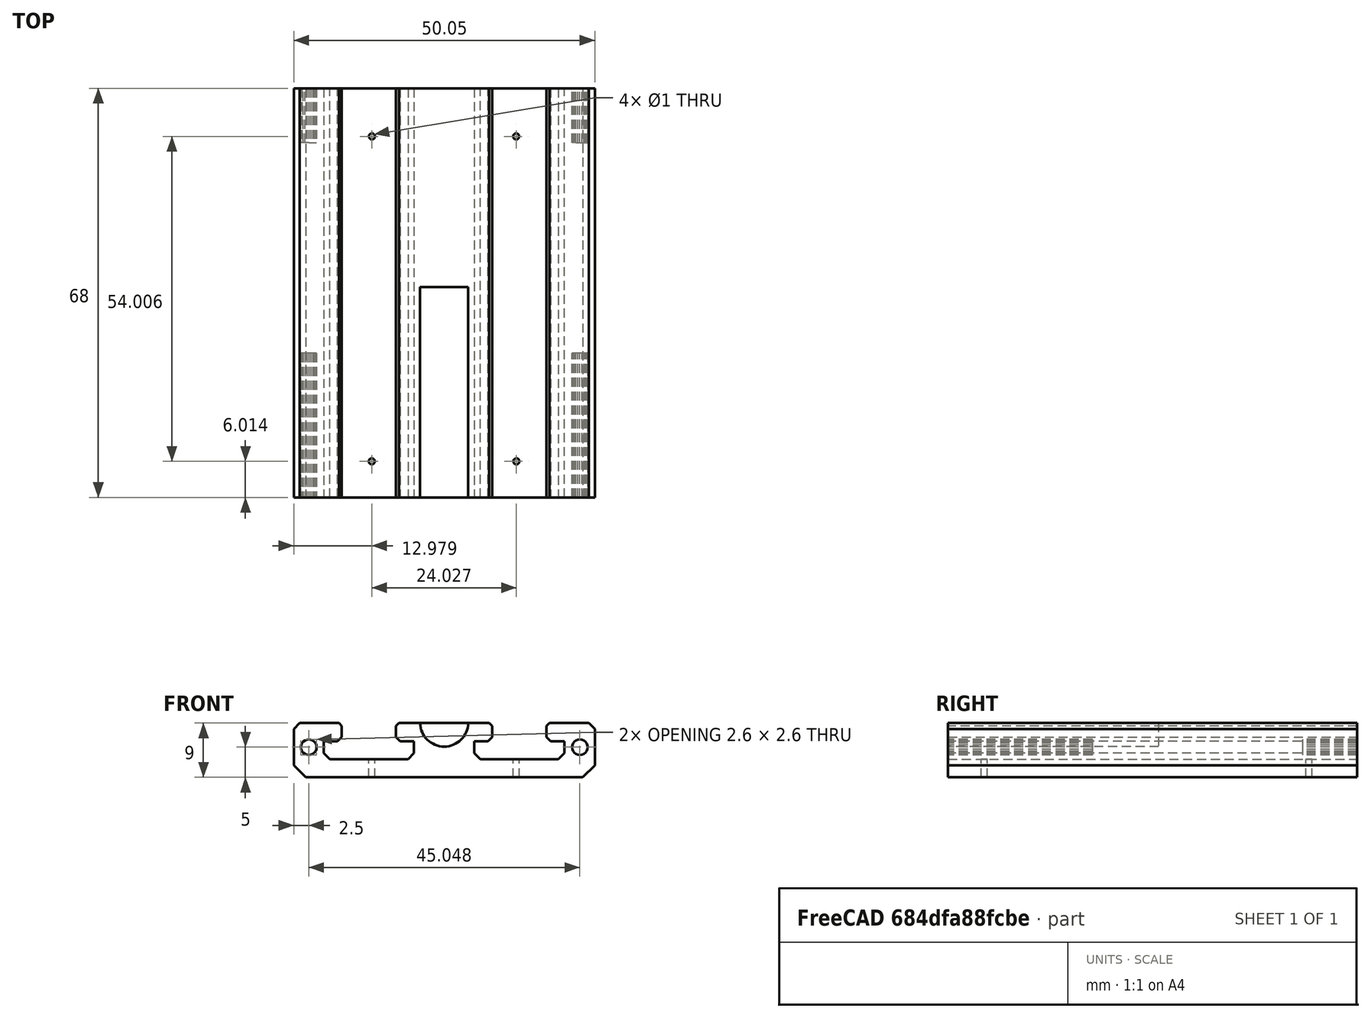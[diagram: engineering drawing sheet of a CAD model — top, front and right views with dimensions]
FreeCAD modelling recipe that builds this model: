
FCSTD DOCUMENT  (FreeCAD 0.21R33771 (Git))
Label: XYstage_Rail
License: All rights reserved
LicenseURL: http://en.wikipedia.org/wiki/All_rights_reserved
objects: Part::Refine×2, PartDesign::FeatureBase×2, PartDesign::Body×2, Sketcher::SketchObject×2, Part::Feature×1, PartDesign::Pad×1, PartDesign::Pocket×1, PartDesign::Hole×1
note: 15 computed .brp shape members not serialized (recipe doc carries the construction recipe); baked Part::Feature solids carry a one-line shape summary decoded from their .brp

FEATURE [Part::Feature] LinearRailTest_Rail_test001_solid  label="LinearRailTest_Rail_test001 (Solid)"
  shape: bbox 50.05 x 53 x 9 mm, 1080 faces (baked)
FEATURE [Part::Refine] LinearRailTest_Rail_test001_solid001  label="LinearRailTest_Rail_test001 (Solid)001"
  Source = -> LinearRailTest_Rail_test001_solid
FEATURE [PartDesign::FeatureBase] BaseFeature
  BaseFeature = -> LinearRailTest_Rail_test001_solid001
FEATURE [PartDesign::Pad] Pad
  BaseFeature = -> BaseFeature
  Direction = (0,-1,0)
  Length = 15
  Length2 = 100
  Profile = -> BaseFeature [Face6]
  Type = 0
FEATURE [PartDesign::Body] Body
  BaseFeature = -> LinearRailTest_Rail_test001_solid001
  Group = -> [BaseFeature,Pad]
  Origin = -> Origin
  Tip = -> Pad
FEATURE [Part::Refine] Body001
  Source = -> Body
FEATURE [Sketcher::SketchObject] Sketch
  AttachmentOffset = pos=(0,0,15) rot=(0,0,1;0rad)
  FullyConstrained = false
  MapMode = 3
  Placement = pos=(0,-15,3.3e-15) rot=(1,0,0;1.5708rad)
  Support = -> [Body001]
  sketch-geometry (1):
    g0: Circle CenterX=0 CenterY=-18.9028 CenterZ=0 NormalX=0 NormalY=0 NormalZ=1 AngleXU=0 Radius=3.9998
  constraints (1):
    c: PointOnObject(g0,g-2)
FEATURE [PartDesign::FeatureBase] BaseFeature001
  BaseFeature = -> Body001
FEATURE [PartDesign::Pocket] Pocket
  BaseFeature = -> BaseFeature001
  Direction = (0,1,-2e-16)
  Length = 35
  Length2 = 5
  Profile = -> Sketch
  ReferenceAxis = -> Sketch [N_Axis]
  Type = 0
FEATURE [Sketcher::SketchObject] Sketch001
  FullyConstrained = false
  MapMode = 5
  Placement = pos=(0,0,-28) rot=(1,0,0;3.14159rad)
  Support = -> [Pocket]
  sketch-geometry (4):
    g0: Circle CenterX=-12.0206 CenterY=8.98552 CenterZ=0 NormalX=0 NormalY=0 NormalZ=1 AngleXU=0 Radius=0.491775
    g1: Circle CenterX=12.0066 CenterY=8.98552 CenterZ=0 NormalX=0 NormalY=0 NormalZ=1 AngleXU=0 Radius=0.506911
    g2: Circle CenterX=-12.0005 CenterY=-45.0206 CenterZ=0 NormalX=0 NormalY=0 NormalZ=1 AngleXU=0 Radius=0.50092
    g3: Circle CenterX=11.9753 CenterY=-45.0161 CenterZ=0 NormalX=0 NormalY=0 NormalZ=1 AngleXU=0 Radius=0.494905
FEATURE [PartDesign::Hole] Hole
  BaseFeature = -> Pocket
  CustomThreadClearance = 0
  Depth = 25
  DepthType = 0
  Diameter = 1
  DrillForDepth = false
  DrillPoint = 1
  DrillPointAngle = 118
  HoleCutCountersinkAngle = 90
  HoleCutCustomValues = false
  HoleCutDepth = 0
  HoleCutDiameter = 6.1
  HoleCutType = 0
  ModelThread = false
  Profile = -> Sketch001
  Tapered = false
  TaperedAngle = 90
  ThreadClass = 0
  ThreadDepth = 25
  ThreadDepthType = 0
  ThreadDirection = 0
  ThreadFit = 0
  ThreadSize = 0
  ThreadType = 0
  Threaded = false
  UseCustomThreadClearance = false
FEATURE [PartDesign::Body] Body002
  BaseFeature = -> Body001
  Group = -> [BaseFeature001,Sketch,Pocket,Sketch001,Hole]
  Origin = -> Origin001
  Tip = -> Hole
